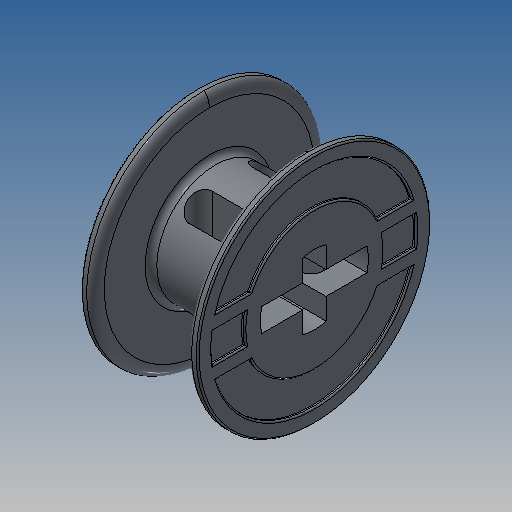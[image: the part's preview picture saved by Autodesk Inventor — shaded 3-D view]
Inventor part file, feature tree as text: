
AUTODESK INVENTOR PART (.ipt)
format: ipt  version: 2025 (Build 290162010, 162A)  size: 423,936 bytes
history: native  units: in
note: dims shown in document units (in); Inventor stores cm internally (conversion verified against a paired STEP export)
features: sketch x3, extrude x3, revolve x1, mirror x1, fillet x1
ambient origin geometry x8: Origin, YZ Plane, XZ Plane, XY Plane, X Axis, Y Axis, Z Axis, Center Point
bodies: Solid1 (feature_tree)
feature tree (9):
  revolve  "Revolution1"  [1 undecoded]
  sketch  "Sketch3"  dims[d2=0.0079in d3=0.378in]
  extrude  "Extrusion1"  Depth=0.378in
  extrude  "Extrusion2"  Depth=0.0039in
  mirror  "Mirror1"
  extrude  "Extrusion3"  Depth=0.0039in
  fillet  "Fillet1"  Radius=0.0157in
  sketch  "Sketch2"  dims[d0=0.6299in d1=0.315in]
  sketch  "Sketch4"  dims[d4=0.5512in d5=0.0315in d6=0.315in d7=0.0157in d8=0.0315in d9=0.0315in d10=0.0157in d11=90.0deg d12=0.189in d13=0.063in d14=0.063in d15=0.2913in d16=0.0787in d17=0.0394in d18=0.3937in d19=0.0in d20=0.3937in d21=0.0in d22=0.063in d23=0.189in d24=0.1102in d25=0.3937in d26=0.0in d27=0.0039in]
note: 1 required parameter value undecoded (feature->parameter linkage not recoverable at this tier; creation-order binding heuristic only, values carry confidence <= 0.55)
